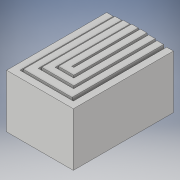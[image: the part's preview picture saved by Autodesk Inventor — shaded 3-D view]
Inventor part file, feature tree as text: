
AUTODESK INVENTOR PART (.ipt)
format: ipt  version: 2017 (Build 210142000, 142)  size: 163,840 bytes
history: native  units: in
note: dims shown in document units (in); Inventor stores cm internally (conversion verified against a paired STEP export)
features: extrude x4, sketch x3
ambient origin geometry x8: Origin, YZ Plane, XZ Plane, XY Plane, X Axis, Y Axis, Z Axis, Center Point
bodies: Solid1 (feature_tree)
feature tree (7):
  sketch  "Sketch1"  dims[d0=20.0in d1=2.0in]
  sketch  "Sketch2"  dims[d2=2.0in d3=30.0in]
  sketch  "Sketch3"  dims[d4=2.0in d5=30.0in d6=0.5in d7=0.5in d8=0.5in d31=2.0in d32=2.0in d33=0.5in d34=0.5in d35=0.5in d36=2.0in d37=2.0in d38=2.0in d39=0.5in d40=0.5in d41=0.5in d42=2.0in d43=2.0in d44=2.0in d45=16.0in d46=0.0in d47=16.25in d48=0.0in d49=16.5in d50=0.0in d51=16.75in d52=0.0in]
  extrude  "Extrusion1"  Depth=2.0in
  extrude  "Extrusion2"  Depth=30.0in
  extrude  "Extrusion3"  Depth=30.0in
  extrude  "Extrusion4"  Depth=0.5in
